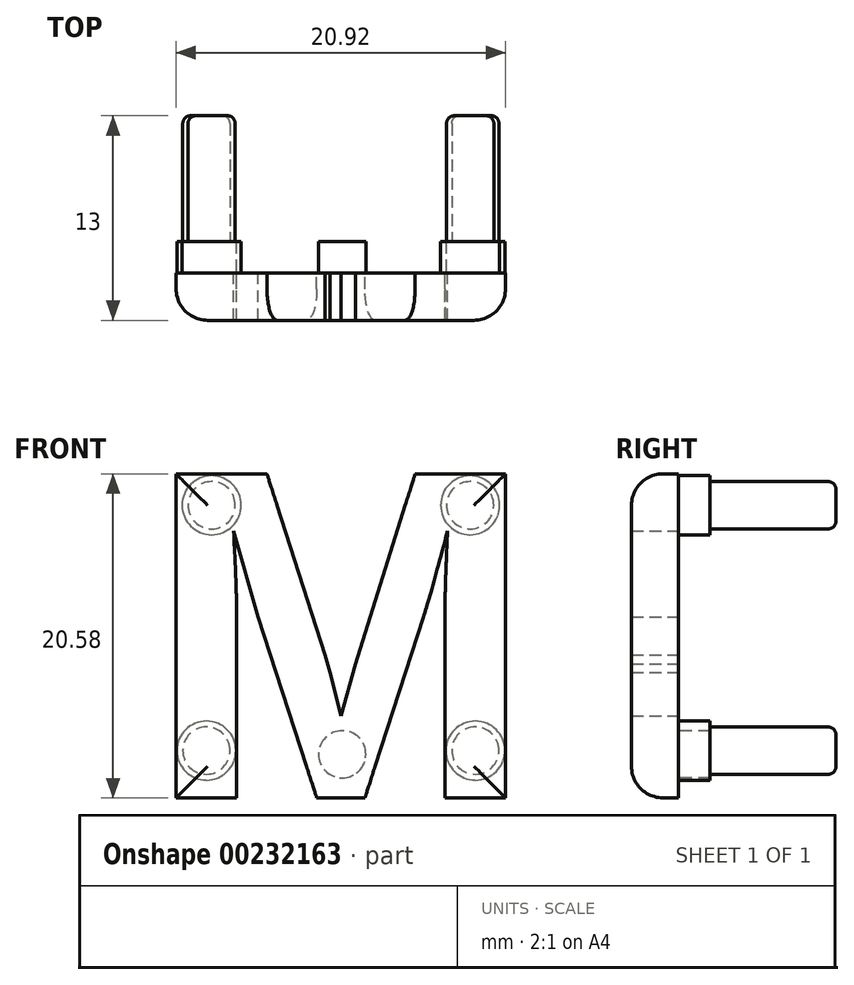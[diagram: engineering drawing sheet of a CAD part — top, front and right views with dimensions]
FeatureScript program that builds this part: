
annotation { "Feature Type Name" : "Feature", "Feature Type Description" : "" }
export const myFeature = defineFeature(function(context is Context, id is Id, definition is map)
    precondition{}
    {
        {
            var Q0;
            Q0=qCreatedBy(makeId("Front.planeOp"),FACE);
            var sketch = newSketch(context, id + "F0", { "sketchPlane" : qUnion([Q0])});
            skText(sketch, "E0", { "text": "M", "fontName": "Arimo-Bold.ttf"});
            const initialGuessF0  = {"E0": [-0.01149, -0.00976, 1, 0, 0.02154]};
            skSetInitialGuess(sketch, initialGuessF0);
            skSolve(sketch);
        }
        {
            var Q0;
            Q0 = qSketchRegion(id + "F0", true);
            extrude(context, id + "F1", {"entities" : qUnion([Q0]), "depth" : 3 * mm});
        }
        {
            var Q0;
            Q0=makeQuery(id+"F1.opExtrude","CAP_FACE",FACE,{"disambiguationData":[OSD([sQuery(id+"F0.wireOp",EDGE,"E0.sketch_text.stroke-0"),sQuery(id+"F0.wireOp",EDGE,"E0.sketch_text.stroke-1"),sQuery(id+"F0.wireOp",EDGE,"E0.sketch_text.stroke-2"),sQuery(id+"F0.wireOp",EDGE,"E0.sketch_text.stroke-3"),sQuery(id+"F0.wireOp",EDGE,"E0.sketch_text.stroke-4"),sQuery(id+"F0.wireOp",EDGE,"E0.sketch_text.stroke-5"),sQuery(id+"F0.wireOp",EDGE,"E0.sketch_text.stroke-6"),sQuery(id+"F0.wireOp",EDGE,"E0.sketch_text.stroke-7"),sQuery(id+"F0.wireOp",EDGE,"E0.sketch_text.stroke-8"),sQuery(id+"F0.wireOp",EDGE,"E0.sketch_text.stroke-9"),sQuery(id+"F0.wireOp",EDGE,"E0.sketch_text.stroke-10"),sQuery(id+"F0.wireOp",EDGE,"E0.sketch_text.stroke-11"),sQuery(id+"F0.wireOp",EDGE,"E0.sketch_text.stroke-12"),sQuery(id+"F0.wireOp",EDGE,"E0.sketch_text.stroke-13"),sQuery(id+"F0.wireOp",EDGE,"E0.sketch_text.stroke-14"),sQuery(id+"F0.wireOp",EDGE,"E0.sketch_text.stroke-15"),sQuery(id+"F0.wireOp",EDGE,"E0.sketch_text.stroke-16"),sQuery(id+"F0.wireOp",EDGE,"E0.sketch_text.stroke-17"),sQuery(id+"F0.wireOp",EDGE,"E0.sketch_text.stroke-18"),sQuery(id+"F0.wireOp",EDGE,"E0.sketch_text.stroke-19"),sQuery(id+"F0.wireOp",EDGE,"E0.sketch_text.stroke-20")])],"isStart":true});
            var sketch = newSketch(context, id + "F2", { "sketchPlane" : qUnion([Q0])});
            skCircle(sketch, "E1", {"center": v(-9.19, 8.82) * mm, "radius": 1.5 * mm});
            skCircle(sketch, "E2", {"center": v(7.23, 8.82) * mm, "radius": 1.5 * mm});
            skCircle(sketch, "E3", {"center": v(7.56, -6.76) * mm, "radius": 1.5 * mm});
            skCircle(sketch, "E4", {"center": v(-9.52, -6.76) * mm, "radius": 1.5 * mm});
            skPoint(sketch, "E5", {"position": v(7.57, -9.76) * mm});
            skSolve(sketch);
        }
        {
            var Q0;
            Q0=makeQuery(id+"F2.imprint","IMPRINT",FACE,{"disambiguationData":[TD([[makeQuery(id+"F2.imprint","IMPRINT",EDGE,{"derivedFrom":sQuery(id+"F2.wireOp",EDGE,"E2")}),1.0]])]});
            var Q1;
            Q1=makeQuery(id+"F2.imprint","IMPRINT",FACE,{"disambiguationData":[TD([[makeQuery(id+"F2.imprint","IMPRINT",EDGE,{"derivedFrom":sQuery(id+"F2.wireOp",EDGE,"E3")}),1.0]])]});
            var Q2;
            Q2=makeQuery(id+"F2.imprint","IMPRINT",FACE,{"disambiguationData":[TD([[makeQuery(id+"F2.imprint","IMPRINT",EDGE,{"derivedFrom":sQuery(id+"F2.wireOp",EDGE,"CFsRcqTr-8Gx7-VYT8-Maol-rQCAMLTUyomC")}),1.0]])]});
            var Q3;
            Q3=makeQuery(id+"F2.imprint","IMPRINT",FACE,{"disambiguationData":[TD([[makeQuery(id+"F2.imprint","IMPRINT",EDGE,{"derivedFrom":sQuery(id+"F2.wireOp",EDGE,"E4")}),1.0]])]});
            var Q4;
            Q4=makeQuery(id+"F2.imprint","IMPRINT",FACE,{"disambiguationData":[TD([[makeQuery(id+"F2.imprint","IMPRINT",EDGE,{"derivedFrom":sQuery(id+"F2.wireOp",EDGE,"E1")}),1.0]])]});
            extrude(context, id + "F3", {"entities" : qUnion([Q0, Q1, Q2, Q3, Q4]), "operationType" : NewBodyOperationType.ADD, "depth" : 10 * mm});
        }
        {
            var Q0;
            Q0=makeQuery(id+"F1.opExtrude","CAP_FACE",FACE,{"disambiguationData":[OSD([sQuery(id+"F0.wireOp",EDGE,"E0.sketch_text.stroke-0"),sQuery(id+"F0.wireOp",EDGE,"E0.sketch_text.stroke-1"),sQuery(id+"F0.wireOp",EDGE,"E0.sketch_text.stroke-2"),sQuery(id+"F0.wireOp",EDGE,"E0.sketch_text.stroke-3"),sQuery(id+"F0.wireOp",EDGE,"E0.sketch_text.stroke-4"),sQuery(id+"F0.wireOp",EDGE,"E0.sketch_text.stroke-5"),sQuery(id+"F0.wireOp",EDGE,"E0.sketch_text.stroke-6"),sQuery(id+"F0.wireOp",EDGE,"E0.sketch_text.stroke-7"),sQuery(id+"F0.wireOp",EDGE,"E0.sketch_text.stroke-8"),sQuery(id+"F0.wireOp",EDGE,"E0.sketch_text.stroke-9"),sQuery(id+"F0.wireOp",EDGE,"E0.sketch_text.stroke-10"),sQuery(id+"F0.wireOp",EDGE,"E0.sketch_text.stroke-11"),sQuery(id+"F0.wireOp",EDGE,"E0.sketch_text.stroke-12"),sQuery(id+"F0.wireOp",EDGE,"E0.sketch_text.stroke-13"),sQuery(id+"F0.wireOp",EDGE,"E0.sketch_text.stroke-14"),sQuery(id+"F0.wireOp",EDGE,"E0.sketch_text.stroke-15"),sQuery(id+"F0.wireOp",EDGE,"E0.sketch_text.stroke-16"),sQuery(id+"F0.wireOp",EDGE,"E0.sketch_text.stroke-17"),sQuery(id+"F0.wireOp",EDGE,"E0.sketch_text.stroke-18"),sQuery(id+"F0.wireOp",EDGE,"E0.sketch_text.stroke-19"),sQuery(id+"F0.wireOp",EDGE,"E0.sketch_text.stroke-20")])],"isStart":true});
            var sketch = newSketch(context, id + "F4", { "sketchPlane" : qUnion([Q0])});
            skCircle(sketch, "E6", {"center": v(-9.19, 8.82) * mm, "radius": 1.88 * mm});
            skCircle(sketch, "E7", {"center": v(7.23, 8.82) * mm, "radius": 1.88 * mm});
            skCircle(sketch, "E8", {"center": v(-1.06, -7) * mm, "radius": 1.5 * mm});
            skCircle(sketch, "E9", {"center": v(-9.52, -6.76) * mm, "radius": 1.88 * mm});
            skCircle(sketch, "E10", {"center": v(7.56, -6.76) * mm, "radius": 1.88 * mm});
            skSolve(sketch);
        }
        {
            var Q0;
            Q0 = qSketchRegion(id + "F4", true);
            extrude(context, id + "F5", {"entities" : qUnion([Q0]), "operationType" : NewBodyOperationType.ADD, "depth" : 2 * mm});
        }
        {
            var Q0;
            Q0=makeQuery(id+"F3.opExtrude","CAP_EDGE",EDGE,{"disambiguationData":[OSD([sQuery(id+"F2.wireOp",EDGE,"E1")])],"isStart":false});
            var Q1;
            Q1=makeQuery(id+"F3.opExtrude","CAP_EDGE",EDGE,{"disambiguationData":[OSD([sQuery(id+"F2.wireOp",EDGE,"E2")])],"isStart":false});
            var Q2;
            Q2=makeQuery(id+"F3.opExtrude","CAP_EDGE",EDGE,{"disambiguationData":[OSD([sQuery(id+"F2.wireOp",EDGE,"E3")])],"isStart":false});
            var Q3;
            Q3=makeQuery(id+"F3.opExtrude","CAP_EDGE",EDGE,{"disambiguationData":[OSD([sQuery(id+"F2.wireOp",EDGE,"CFsRcqTr-8Gx7-VYT8-Maol-rQCAMLTUyomC")])],"isStart":false});
            var Q4;
            Q4=makeQuery(id+"F3.opExtrude","CAP_EDGE",EDGE,{"disambiguationData":[OSD([sQuery(id+"F2.wireOp",EDGE,"E4")])],"isStart":false});
            fillet(context, id + "F6", {"entities" : qUnion([Q0, Q1, Q2, Q3, Q4]), "radius" : 0.5 * mm, "tangentPropagation" : true, "allowEdgeOverflow" : false});
        }
        {
            var Q0;
            Q0=makeQuery(id+"F1.opExtrude","CAP_EDGE",EDGE,{"disambiguationData":[OSD([sQuery(id+"F0.wireOp",EDGE,"E0.sketch_text.stroke-19")])],"isStart":false});
            var Q1;
            Q1=makeQuery(id+"F1.opExtrude","CAP_EDGE",EDGE,{"disambiguationData":[OSD([sQuery(id+"F0.wireOp",EDGE,"E0.sketch_text.stroke-18")])],"isStart":false});
            var Q2;
            Q2=makeQuery(id+"F1.opExtrude","CAP_EDGE",EDGE,{"disambiguationData":[OSD([sQuery(id+"F0.wireOp",EDGE,"E0.sketch_text.stroke-20")])],"isStart":false});
            var Q3;
            Q3=makeQuery(id+"F1.opExtrude","CAP_EDGE",EDGE,{"disambiguationData":[OSD([sQuery(id+"F0.wireOp",EDGE,"E0.sketch_text.stroke-12")])],"isStart":false});
            var Q4;
            Q4=makeQuery(id+"F1.opExtrude","CAP_EDGE",EDGE,{"disambiguationData":[OSD([sQuery(id+"F0.wireOp",EDGE,"E0.sketch_text.stroke-11")])],"isStart":false});
            var Q5;
            Q5=makeQuery(id+"F1.opExtrude","CAP_EDGE",EDGE,{"disambiguationData":[OSD([sQuery(id+"F0.wireOp",EDGE,"E0.sketch_text.stroke-10")])],"isStart":false});
            var Q6;
            Q6=makeQuery(id+"F1.opExtrude","CAP_EDGE",EDGE,{"disambiguationData":[OSD([sQuery(id+"F0.wireOp",EDGE,"E0.sketch_text.stroke-5")])],"isStart":false});
            fillet(context, id + "F7", {"entities" : qUnion([Q0, Q1, Q2, Q3, Q4, Q5, Q6]), "radius" : 2 * mm, "tangentPropagation" : true, "allowEdgeOverflow" : false});
        }
    });
